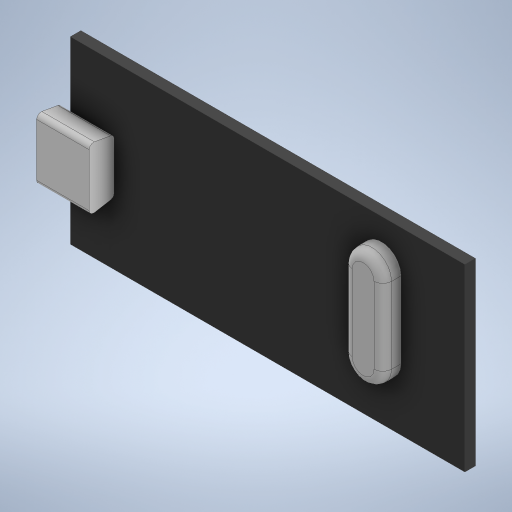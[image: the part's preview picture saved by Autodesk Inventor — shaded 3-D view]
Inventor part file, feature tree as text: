
AUTODESK INVENTOR PART (.ipt)
format: ipt  version: 2023.1 (Build 271208000, 208)  size: 311,296 bytes
history: native  units: mm
features: extrude x4, sketch x4, other x1, fillet x1, projected_geometry x1
ambient origin geometry x8: Origin, YZ Plane, XZ Plane, XY Plane, X Axis, Y Axis, Z Axis, Center Point
bodies: Body1 (feature_tree)
feature tree (11):
  other  "솔리드1"
  extrude  "돌출1"  Depth=45.0mm
  extrude  "돌출2"  Depth=20.5mm
  extrude  "돌출3"  Depth=1.2mm TaperAngle=0.0deg
  extrude  "돌출4"  Depth=2.85mm
  fillet  "모깎기1"  Radius=7.2mm
  sketch  "스케치1"
  sketch  "스케치2"
  sketch  "스케치3"
  projected_geometry  "투영된 루프1"
  sketch  "스케치4"
